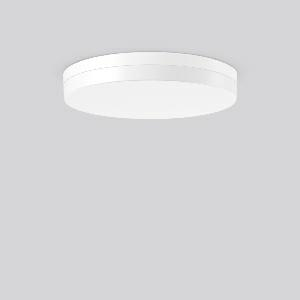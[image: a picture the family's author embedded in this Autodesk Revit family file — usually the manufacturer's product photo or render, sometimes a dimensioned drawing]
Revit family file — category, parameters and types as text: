
# Revit family: flat_slim_round_312634_002_1_19_035c
name_source: partatom
category: Lighting Fixtures
units: mm (PartAtom-declared; Revit-internal decimal feet)

## family parameters
Cut with Voids When Loaded = No
Host = Face
Light Source = No
Part Type = Normal
Room Calculation Point = No
Round Connector Dimension = Use Diameter
Shared = No

## types (1)
- MultiLumen 1 830 (1 x LED Modul 830, 3500 lm, 3000)
    Apparent Load = 24 VA
    CIE Flux Codes = 38 68 89 85 100
    Color Rendering = 80
    Color Temperature = 3000
    Default Elevation = 1800 mm
    Height = 70 mm
    Lamp = 1 x LED Modul 830
    Lamp Light Flux = 3500 lm
    Lamp count = 1
    Length = 480 mm
    Lifetime = 50000 h
    Luminous efficacy = 146 lm/W
    Manufacturer = RZB
    ModVariant = No
    Model = 312634.002.1.19
    Mounting Place = Ceiling
    Mounting Type = Surface mounted
    Number of Poles = 1
    OnlyDefault = Yes
    Power Factor = 1
    Product Name = FLAT SLIM round
    Product group = Surface mounted ceiling and wall luminaires
    ProductGroupID = 305
    Protection Class = Protection class I
    Protection Degree = Degree of protection
    RLX_Detail_Level = 1
    RLX_Emergency_Light_Flux = 0 lm
    RLX_Emergency_Type = 0
    RLX_Emergency_Type_DB = No
    RlxData = <blob elided: 22073 chars, md5=66e2664b>
    Socket = socket
    Standby Power = 0 W
    System Light Flux = 3500 lm
    System Power = 24 W
    Type Comments = MultiLumen 1 830
    Type Image = 312633.002.jpg
    URL = http://relux.com
    VarID = multilumen_1_830
    Voltage = 0 V
    Weight = 0.00 kg
    Width = 0 mm  [stored 0 ft]

note: [stored X ft] marks values corroborated as IEEE doubles in the binary element streams (Revit-internal decimal feet)

## geometry (parser evidence)
native form markers: Blend x4, Sweep x13
no freeform markers — native parametric forms only
